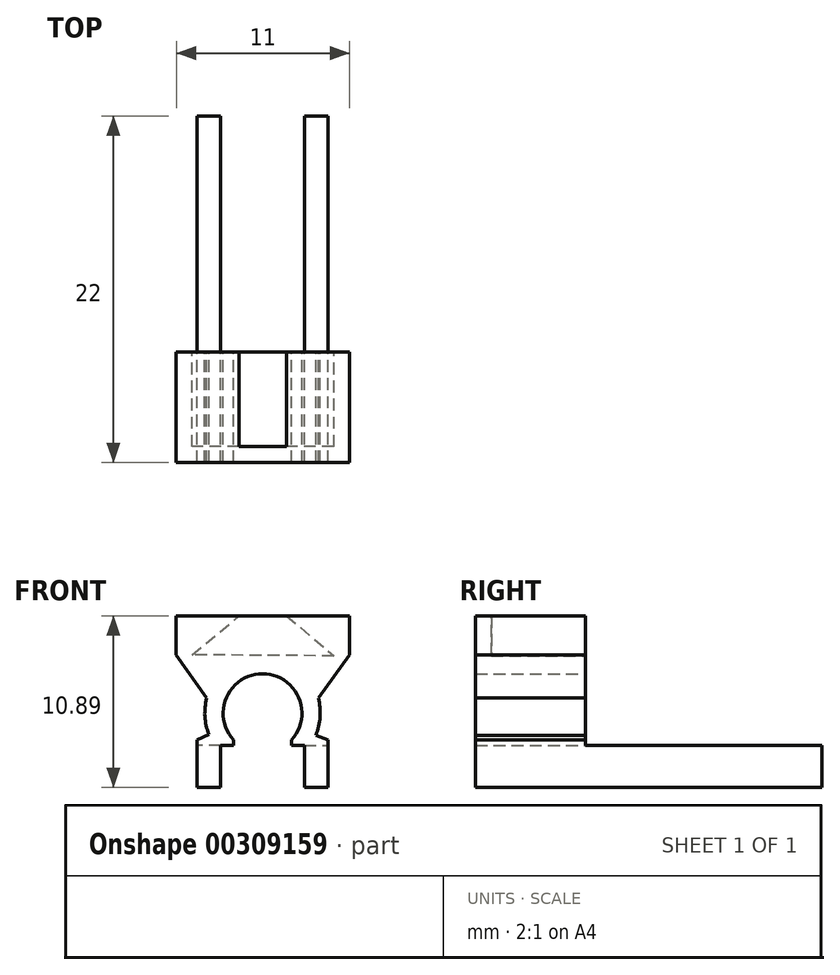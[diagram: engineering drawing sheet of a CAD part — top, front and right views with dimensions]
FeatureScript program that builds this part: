
annotation { "Feature Type Name" : "Feature", "Feature Type Description" : "" }
export const myFeature = defineFeature(function(context is Context, id is Id, definition is map)
    precondition{}
    {
        {
            var Q0;
            Q0=qCreatedBy(makeId("Front.planeOp"),FACE);
            var sketch = newSketch(context, id + "F0", { "sketchPlane" : qUnion([Q0])});
            skLineSegment(sketch, "E0", {"start": v(-3.34, -1.58) * mm, "end": v(-3.32, -1.6) * mm});
            skArc(sketch, "E1.trimOffspring", {"start": v(3.45, -1.63) * mm, "mid": v(0.1, 3.44) * mm, "end": v(-3.34, -1.58) * mm});
            skLineSegment(sketch, "E2", {"start": v(-3.32, -1.6) * mm, "end": v(-3.32, -2.28) * mm});
            skLineSegment(sketch, "E3", {"start": v(-3.32, -4.95) * mm, "end": v(-2.59, -4.95) * mm});
            skLineSegment(sketch, "E4", {"start": v(3.45, -1.63) * mm, "end": v(3.45, -2.28) * mm});
            skLineSegment(sketch, "E5", {"start": v(3.45, -4.95) * mm, "end": v(2.72, -4.95) * mm});
            skLineSegment(sketch, "E6", {"start": v(-4.09, -1.94) * mm, "end": v(-4.09, -4.95) * mm});
            skLineSegment(sketch, "E7", {"start": v(-4.09, -4.95) * mm, "end": v(-3.32, -4.95) * mm});
            skLineSegment(sketch, "E8.MirrorCS", {"start": v(4.22, -1.94) * mm, "end": v(4.22, -4.95) * mm});
            skLineSegment(sketch, "E9.MirrorCS", {"start": v(4.22, -4.95) * mm, "end": v(3.45, -4.95) * mm});
            skLineSegment(sketch, "E10", {"start": v(-4.09, -1.94) * mm, "end": v(-3.32, -1.6) * mm});
            skLineSegment(sketch, "E11", {"start": v(4.22, -1.94) * mm, "end": v(3.45, -1.63) * mm});
            skLineSegment(sketch, "E12", {"start": v(0.1, 3.44) * mm, "end": v(-4.4, 3.47) * mm});
            skLineSegment(sketch, "E13", {"start": v(0.1, 3.44) * mm, "end": v(4.6, 3.4) * mm});
            skLineSegment(sketch, "E14", {"start": v(0.1, 3.44) * mm, "end": v(0.1, 5.94) * mm, "construction": true});
            skLineSegment(sketch, "E15", {"start": v(-4.4, 3.47) * mm, "end": v(-1.41, 5.94) * mm});
            skLineSegment(sketch, "E16", {"start": v(1.6, 5.94) * mm, "end": v(4.6, 3.4) * mm});
            skLineSegment(sketch, "E17", {"start": v(-1.41, 5.94) * mm, "end": v(-5.41, 5.94) * mm});
            skLineSegment(sketch, "E18", {"start": v(-5.41, 5.94) * mm, "end": v(-5.41, 3.47) * mm});
            skLineSegment(sketch, "E19", {"start": v(-5.41, 3.47) * mm, "end": v(-3.48, 0.72) * mm});
            skLineSegment(sketch, "E20", {"start": v(1.6, 5.94) * mm, "end": v(5.59, 5.94) * mm});
            skLineSegment(sketch, "E21", {"start": v(5.59, 5.94) * mm, "end": v(5.59, 3.47) * mm});
            skLineSegment(sketch, "E22", {"start": v(5.59, 3.47) * mm, "end": v(3.6, 0.72) * mm});
            skLineSegment(sketch, "E23", {"start": v(-1.41, 5.94) * mm, "end": v(1.6, 5.94) * mm});
            skLineSegment(sketch, "E24", {"start": v(-3.32, -2.28) * mm, "end": v(-4.09, -2.28) * mm});
            skLineSegment(sketch, "E25", {"start": v(3.45, -2.28) * mm, "end": v(4.22, -2.28) * mm});
            skLineSegment(sketch, "E26", {"start": v(3.45, -2.28) * mm, "end": v(3.45, -4.95) * mm, "construction": true});
            skLineSegment(sketch, "E27.0", {"start": v(2.72, -2.28) * mm, "end": v(2.72, -4.95) * mm});
            skLineSegment(sketch, "E28.0", {"start": v(-2.59, -2.28) * mm, "end": v(-2.59, -4.95) * mm});
            skLineSegment(sketch, "E29", {"start": v(-2.59, -2.28) * mm, "end": v(-3.32, -2.28) * mm});
            skLineSegment(sketch, "E30", {"start": v(2.72, -2.28) * mm, "end": v(3.45, -2.28) * mm});
            skPoint(sketch, "E31.orphan", {"position": v(-1.76, -2.28) * mm});
            skPoint(sketch, "E32.orphan", {"position": v(1.9, -2.28) * mm});
            skArc(sketch, "E33", {"start": v(1.9, -1.93) * mm, "mid": v(0.06, 2.27) * mm, "end": v(-1.76, -1.93) * mm});
            skLineSegment(sketch, "E34", {"start": v(2.72, -2.28) * mm, "end": v(1.9, -2.28) * mm});
            skLineSegment(sketch, "E35", {"start": v(1.9, -2.28) * mm, "end": v(1.9, -1.93) * mm});
            skLineSegment(sketch, "E36", {"start": v(-2.59, -2.28) * mm, "end": v(-1.76, -2.28) * mm});
            skLineSegment(sketch, "E37", {"start": v(-1.76, -1.93) * mm, "end": v(-1.76, -2.28) * mm});
            skSolve(sketch);
        }
        {
            var Q0;
            Q0=qSketchRegion(id+"F0",true);
            extrude(context, id + "F1", {"entities" : qUnion([Q0]), "depth" : 7 * mm});
        }
        {
            var Q0;
            Q0=makeQuery(id+"F0.imprint","IMPRINT",FACE,{"disambiguationData":[TD([[makeQuery(id+"F0.imprint","IMPRINT",EDGE,{"derivedFrom":sQuery(id+"F0.wireOp",EDGE,"E12")}),-1.0]])]});
            extrude(context, id + "F2", {"entities" : qUnion([Q0]), "operationType" : NewBodyOperationType.REMOVE, "depth" : 6 * mm});
        }
        {
            var Q0;
            Q0=makeQuery(id+"F0.imprint","IMPRINT",FACE,{"disambiguationData":[TD([[makeQuery(id+"F0.imprint","IMPRINT",EDGE,{"derivedFrom":sQuery(id+"F0.wireOp",EDGE,"E5")}),-1.0]])]});
            var Q1;
            Q1=makeQuery(id+"F0.imprint","IMPRINT",FACE,{"disambiguationData":[TD([[makeQuery(id+"F0.imprint","IMPRINT",EDGE,{"derivedFrom":sQuery(id+"F0.wireOp",EDGE,"E3")}),1.0]])]});
            extrude(context, id + "F3", {"entities" : qUnion([Q0, Q1]), "operationType" : NewBodyOperationType.ADD, "oppositeDirection" : true, "depth" : 15 * mm, "offsetDistance" : 25 * mm});
        }
    });
